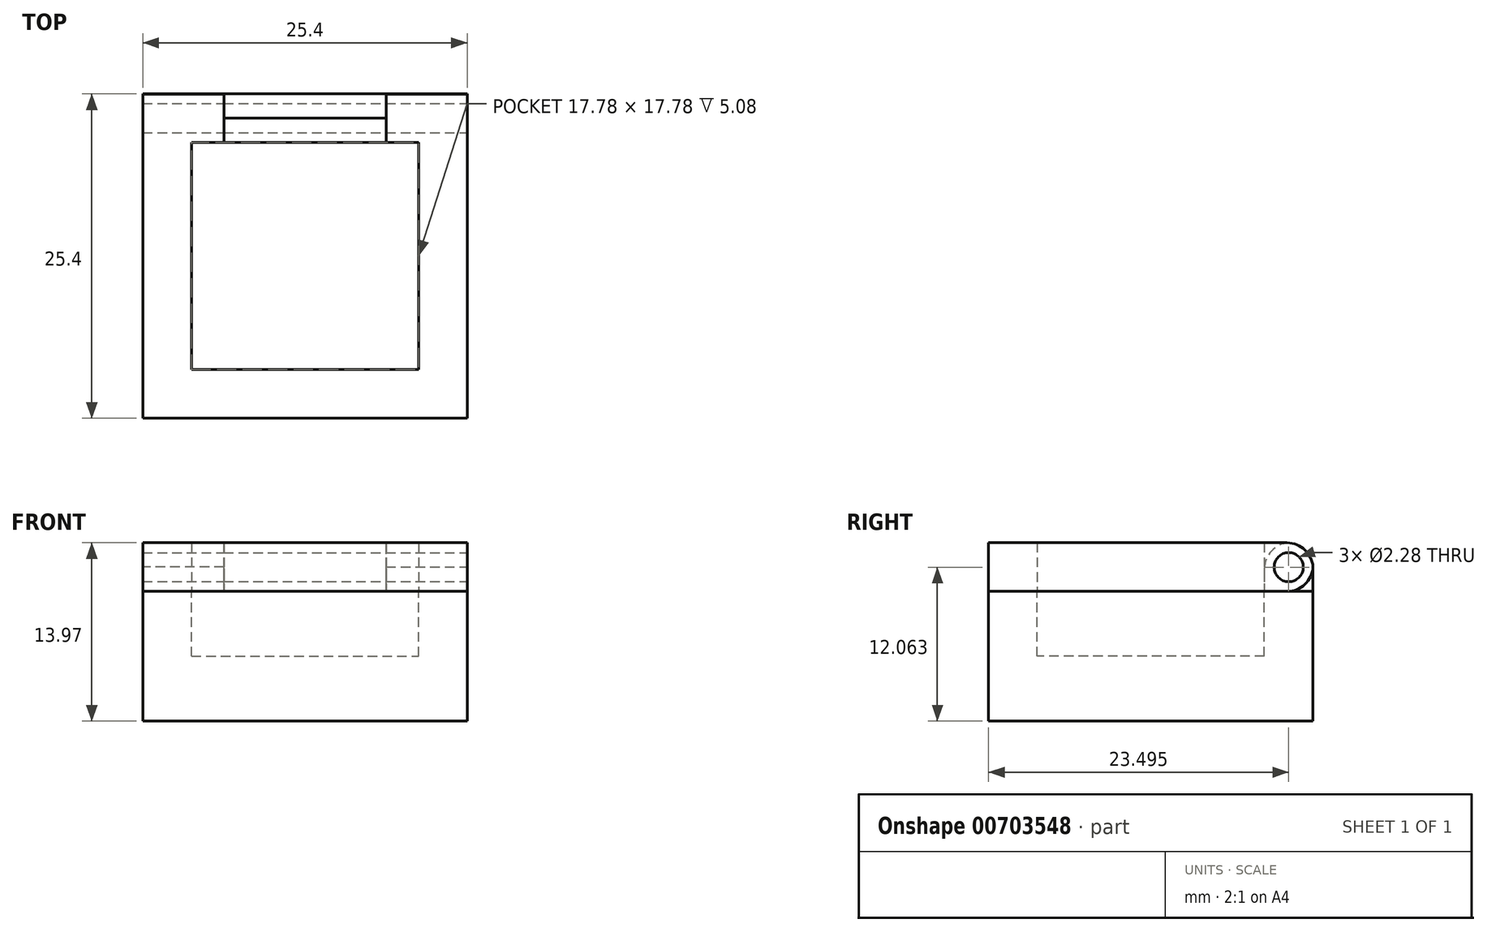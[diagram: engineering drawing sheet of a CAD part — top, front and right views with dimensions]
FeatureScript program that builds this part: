
annotation { "Feature Type Name" : "Feature", "Feature Type Description" : "" }
export const myFeature = defineFeature(function(context is Context, id is Id, definition is map)
    precondition{}
    {
        {
            var Q0;
            Q0=qCreatedBy(makeId("Top.planeOp"),FACE);
            var sketch = newSketch(context, id + "F0", { "sketchPlane" : qUnion([Q0])});
            skLineSegment(sketch, "E0.bottom", {"start": v(0, 0) * mm, "end": v(25.4, 0) * mm});
            skLineSegment(sketch, "E0.top", {"start": v(0, 25.4) * mm, "end": v(25.4, 25.4) * mm});
            skLineSegment(sketch, "E0.left", {"start": v(0, 0) * mm, "end": v(0, 25.4) * mm});
            skLineSegment(sketch, "E0.right", {"start": v(25.4, 0) * mm, "end": v(25.4, 25.4) * mm});
            skSolve(sketch);
        }
        {
            var Q0;
            Q0=makeQuery(id+"F0.imprint","IMPRINT",FACE,{"disambiguationData":[TD([[makeQuery(id+"F0.imprint","IMPRINT",EDGE,{"derivedFrom":sQuery(id+"F0.wireOp",EDGE,"E0.bottom")}),1.0]])]});
            extrude(context, id + "F1", {"entities" : qUnion([Q0]), "depth" : 10.16 * mm, "offsetDistance" : 25.4 * mm});
        }
        {
            var Q0;
            Q0=makeQuery(id+"F1.opExtrude","CAP_FACE",FACE,{"disambiguationData":[OSD([sQuery(id+"F0.wireOp",EDGE,"E0.bottom"),sQuery(id+"F0.wireOp",EDGE,"E0.top"),sQuery(id+"F0.wireOp",EDGE,"E0.left"),sQuery(id+"F0.wireOp",EDGE,"E0.right")])],"isStart":false});
            var sketch = newSketch(context, id + "F2", { "sketchPlane" : qUnion([Q0])});
            skLineSegment(sketch, "E1.bottom", {"start": v(3.8, 21.59) * mm, "end": v(21.59, 21.59) * mm});
            skLineSegment(sketch, "E1.top", {"start": v(3.81, 3.81) * mm, "end": v(21.59, 3.81) * mm});
            skLineSegment(sketch, "E1.left", {"start": v(3.8, 21.59) * mm, "end": v(3.81, 3.81) * mm});
            skLineSegment(sketch, "E1.right", {"start": v(21.59, 21.59) * mm, "end": v(21.59, 3.81) * mm});
            skSolve(sketch);
        }
        {
            var Q0;
            Q0=makeQuery(id+"F2.imprint","IMPRINT",FACE,{"disambiguationData":[TD([[makeQuery(id+"F2.imprint","IMPRINT",EDGE,{"derivedFrom":sQuery(id+"F2.wireOp",EDGE,"E1.bottom")}),-1.0]])]});
            extrude(context, id + "F3", {"entities" : qUnion([Q0]), "operationType" : NewBodyOperationType.REMOVE, "oppositeDirection" : true, "depth" : 5.08 * mm, "offsetDistance" : 25.4 * mm});
        }
        {
            var Q0;
            Q0=makeQuery(id+"F1.opExtrude","CAP_FACE",FACE,{"disambiguationData":[OSD([sQuery(id+"F0.wireOp",EDGE,"E0.bottom"),sQuery(id+"F0.wireOp",EDGE,"E0.top"),sQuery(id+"F0.wireOp",EDGE,"E0.left"),sQuery(id+"F0.wireOp",EDGE,"E0.right")])],"isStart":false});
            var sketch = newSketch(context, id + "F4", { "sketchPlane" : qUnion([Q0])});
            skLineSegment(sketch, "E2.bottom", {"start": v(0, 25.4) * mm, "end": v(6.35, 25.4) * mm});
            skLineSegment(sketch, "E2.top", {"start": v(0, 21.59) * mm, "end": v(6.35, 21.59) * mm});
            skLineSegment(sketch, "E2.left", {"start": v(0, 25.4) * mm, "end": v(0, 21.59) * mm});
            skLineSegment(sketch, "E2.right", {"start": v(6.35, 25.4) * mm, "end": v(6.35, 21.59) * mm});
            skLineSegment(sketch, "E3", {"start": v(12.7, 25.4) * mm, "end": v(12.7, 0) * mm});
            skLineSegment(sketch, "E4.MirrorCS", {"start": v(19.05, 25.4) * mm, "end": v(19.05, 21.59) * mm});
            skLineSegment(sketch, "E5.MirrorCS", {"start": v(25.4, 21.59) * mm, "end": v(19.05, 21.59) * mm});
            skLineSegment(sketch, "E6.MirrorCS", {"start": v(25.4, 25.4) * mm, "end": v(25.4, 21.59) * mm});
            skLineSegment(sketch, "E7.MirrorCS", {"start": v(25.4, 25.4) * mm, "end": v(19.05, 25.4) * mm});
            skSolve(sketch);
        }
        {
            var Q0;
            {var subQ0=sQuery(id+"F4.wireOp",EDGE,"E2.right");Q0=makeQuery(id+"F4.imprint","IMPRINT",FACE,{"disambiguationData":[TD([[makeQuery(id+"F4.imprint","IMPRINT",EDGE,{"derivedFrom":subQ0}),1.0]])]});}
            var Q1;
            {var subQ5=sQuery(id+"F4.wireOp",EDGE,"E4.MirrorCS");Q1=makeQuery(id+"F4.imprint","IMPRINT",FACE,{"disambiguationData":[TD([[makeQuery(id+"F4.imprint","IMPRINT",EDGE,{"derivedFrom":subQ5}),-1.0]])]});}
            extrude(context, id + "F5", {"entities" : qUnion([Q0, Q1]), "operationType" : NewBodyOperationType.ADD, "depth" : 3.8 * mm, "offsetDistance" : 25.4 * mm});
        }
        {
            var Q0;
            Q0=makeQuery(id+"F1.opExtrude","CAP_FACE",FACE,{"disambiguationData":[OSD([sQuery(id+"F0.wireOp",EDGE,"E0.bottom"),sQuery(id+"F0.wireOp",EDGE,"E0.top"),sQuery(id+"F0.wireOp",EDGE,"E0.left"),sQuery(id+"F0.wireOp",EDGE,"E0.right")])],"isStart":false});
            var sketch = newSketch(context, id + "F6", { "sketchPlane" : qUnion([Q0])});
            skLineSegment(sketch, "E8.bottom", {"start": v(0, 21.59) * mm, "end": v(25.4, 21.59) * mm});
            skLineSegment(sketch, "E8.top", {"start": v(0, 0) * mm, "end": v(25.4, 0) * mm});
            skLineSegment(sketch, "E8.left", {"start": v(0, 21.59) * mm, "end": v(0, 0) * mm});
            skLineSegment(sketch, "E8.right", {"start": v(25.4, 21.59) * mm, "end": v(25.4, 0) * mm});
            skLineSegment(sketch, "E9.bottom", {"start": v(0, 25.4) * mm, "end": v(6.35, 25.4) * mm});
            skLineSegment(sketch, "E9.top", {"start": v(0, 21.59) * mm, "end": v(6.35, 21.59) * mm});
            skLineSegment(sketch, "E9.left", {"start": v(0, 25.4) * mm, "end": v(0, 21.59) * mm});
            skLineSegment(sketch, "E9.right", {"start": v(6.35, 25.4) * mm, "end": v(6.35, 21.59) * mm});
            skLineSegment(sketch, "E10.bottom", {"start": v(19.05, 25.4) * mm, "end": v(25.4, 25.4) * mm});
            skLineSegment(sketch, "E10.top", {"start": v(19.05, 21.59) * mm, "end": v(25.4, 21.59) * mm});
            skLineSegment(sketch, "E10.left", {"start": v(19.05, 25.4) * mm, "end": v(19.05, 21.59) * mm});
            skLineSegment(sketch, "E10.right", {"start": v(25.4, 25.4) * mm, "end": v(25.4, 21.59) * mm});
            skSolve(sketch);
        }
        {
            var Q0;
            Q0=makeQuery(id+"F6.imprint","IMPRINT",FACE,{"disambiguationData":[TD([[makeQuery(id+"F6.imprint","IMPRINT",EDGE,{"derivedFrom":sQuery(id+"F6.wireOp",EDGE,"E8.top")}),1.0]])]});
            var Q1;
            Q1=makeQuery(id+"F6.imprint","IMPRINT",FACE,{"disambiguationData":[TD([[makeQuery(id+"F6.imprint","IMPRINT",EDGE,{"derivedFrom":makeQuery(id+"F3.boolean.opBoolean","COPY",EDGE,{"derivedFrom":makeQuery(id+"F3.opExtrude","CAP_EDGE",EDGE,{"disambiguationData":[OSD([sQuery(id+"F2.wireOp",EDGE,"E1.top")])],"isStart":true})})}),1.0]])]});
            var Q2;
            Q2=makeQuery(id+"F6.imprint","IMPRINT",FACE,{"disambiguationData":[TD([[makeQuery(id+"F6.imprint","IMPRINT",EDGE,{"derivedFrom":sQuery(id+"F6.wireOp",EDGE,"E10.bottom")}),-1.0]])]});
            var Q3;
            Q3=makeQuery(id+"F6.imprint","IMPRINT",FACE,{"disambiguationData":[TD([[makeQuery(id+"F6.imprint","IMPRINT",EDGE,{"derivedFrom":sQuery(id+"F6.wireOp",EDGE,"E9.bottom")}),-1.0]])]});
            extrude(context, id + "F7", {"entities" : qUnion([Q0, Q1, Q2, Q3]), "depth" : 3.8 * mm, "offsetDistance" : 25.4 * mm});
        }
        {
            var Q0;
            Q0=makeQuery(id+"F7.opExtrude","CAP_EDGE",EDGE,{"disambiguationData":[OSD([sQuery(id+"F6.wireOp",EDGE,"E9.bottom")])],"isStart":true});
            var Q1;
            Q1=makeQuery(id+"F7.opExtrude","CAP_EDGE",EDGE,{"disambiguationData":[OSD([sQuery(id+"F6.wireOp",EDGE,"E10.bottom")])],"isStart":false});
            var Q2;
            Q2=makeQuery(id+"F7.opExtrude","CAP_EDGE",EDGE,{"disambiguationData":[OSD([sQuery(id+"F6.wireOp",EDGE,"E10.bottom")])],"isStart":true});
            var Q3;
            Q3=makeQuery(id+"F7.opExtrude","CAP_EDGE",EDGE,{"disambiguationData":[OSD([sQuery(id+"F6.wireOp",EDGE,"E9.bottom")])],"isStart":false});
            fillet(context, id + "F8", {"entities" : qUnion([Q0, Q1, Q2, Q3]), "radius" : 2.03 * mm, "tangentPropagation" : true, "allowEdgeOverflow" : false});
        }
        {
            var Q0;
            Q0=makeQuery(id+"F5.opExtrude","CAP_EDGE",EDGE,{"disambiguationData":[OSD([sQuery(id+"F2.wireOp",EDGE,"E1.bottom")])],"isStart":false});
            var Q1;
            Q1=makeQuery(id+"F5.opExtrude","CAP_EDGE",EDGE,{"disambiguationData":[OSD([sQuery(id+"F0.wireOp",EDGE,"E0.top")])],"isStart":false});
            fillet(context, id + "F9", {"entities" : qUnion([Q0, Q1]), "radius" : 2.03 * mm, "tangentPropagation" : true, "allowEdgeOverflow" : false});
        }
        {
            var Q0;
            Q0=makeQuery(id+"F7.opExtrude","SWEPT_FACE",FACE,{"disambiguationData":[OSD([sQuery(id+"F6.wireOp",EDGE,"E8.right"),sQuery(id+"F6.wireOp",EDGE,"E10.right")])]});
            var sketch = newSketch(context, id + "F10", { "sketchPlane" : qUnion([Q0])});
            skCircle(sketch, "E11", {"center": v(23.5, 12.06) * mm, "radius": 1.14 * mm});
            skSolve(sketch);
        }
        {
            var Q0;
            Q0=makeQuery(id+"F10.imprint","IMPRINT",FACE,{"disambiguationData":[TD([[makeQuery(id+"F10.imprint","IMPRINT",EDGE,{"derivedFrom":sQuery(id+"F10.wireOp",EDGE,"E11")}),1.0]])]});
            extrude(context, id + "F11", {"entities" : qUnion([Q0]), "operationType" : NewBodyOperationType.REMOVE, "oppositeDirection" : true, "depth" : 25.4 * mm, "offsetDistance" : 25.4 * mm});
        }
    });
